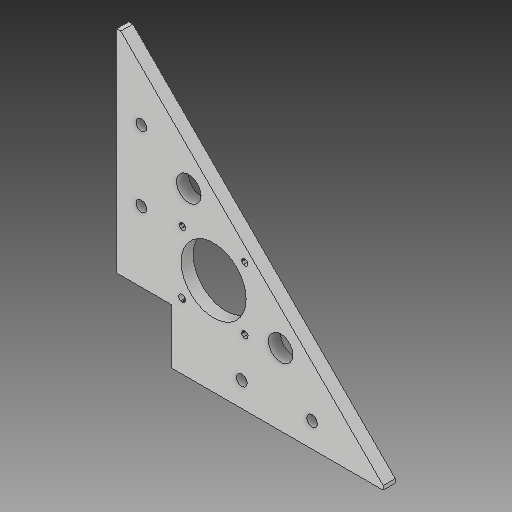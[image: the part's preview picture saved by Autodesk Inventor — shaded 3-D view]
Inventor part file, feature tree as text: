
AUTODESK INVENTOR PART (.ipt)
format: ipt  version: 2018 (Build 220112000, 112)  size: 253,440 bytes
history: native  units: mm
features: other x3, sketch x2
ambient origin geometry x8: Origin, YZ Plane, XZ Plane, XY Plane, X Axis, Y Axis, Z Axis, Center Point
bodies: Solid1 (feature_tree)
feature tree (5):
  other  "Z Motor Mount Right.ipt"
  other  "Solid1::Z Motor Mount Right.ipt"
  other  "TaggingFeature1"
  sketch  "Sketch1"  dims[d0=10.0mm]
  sketch  "Sketch2"
